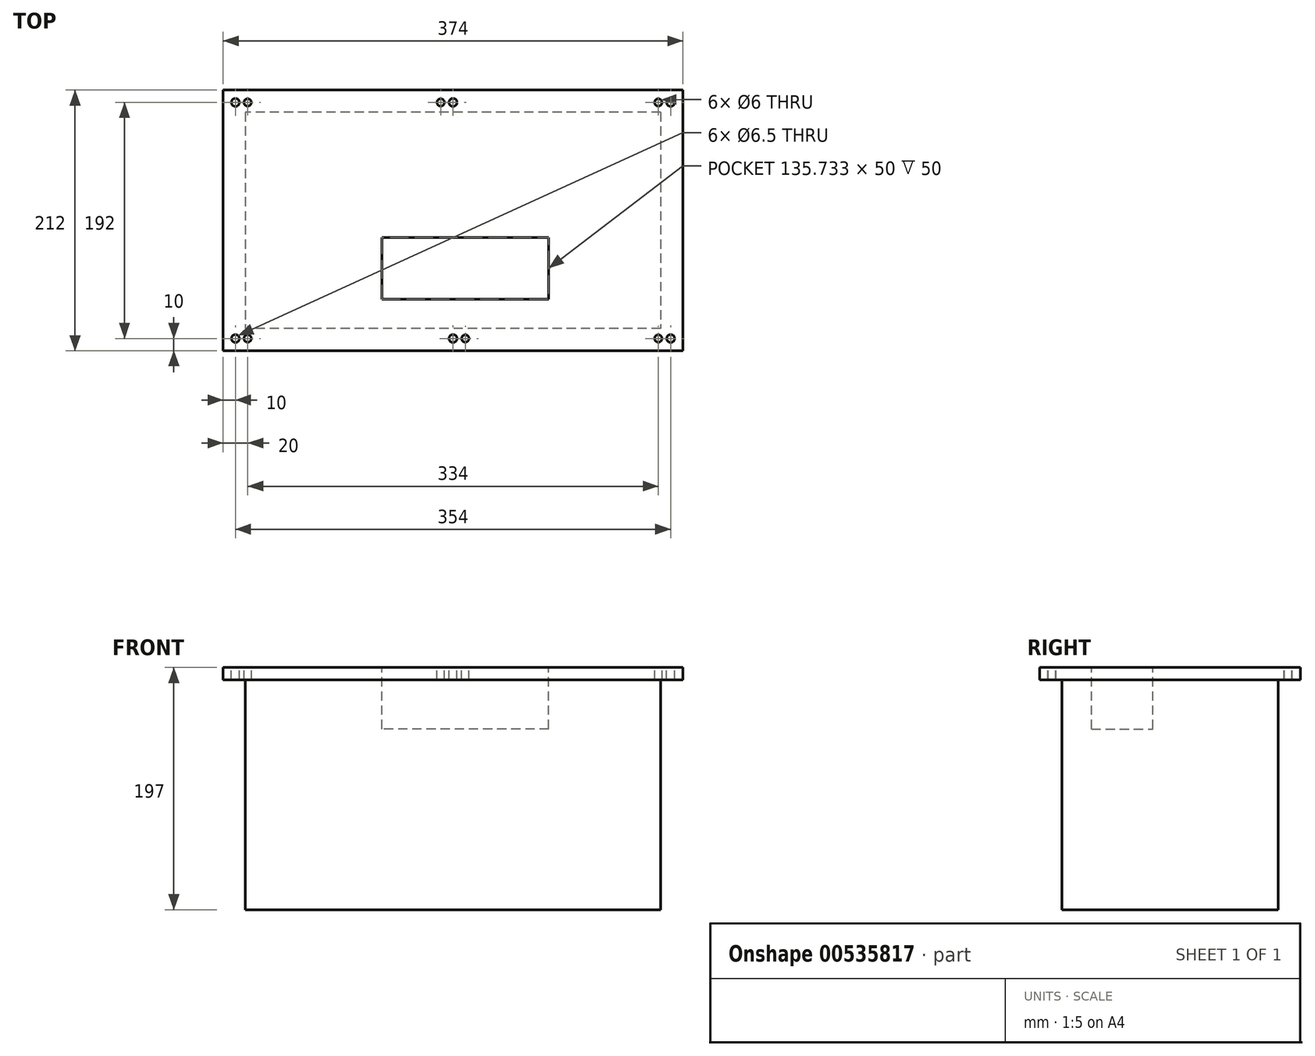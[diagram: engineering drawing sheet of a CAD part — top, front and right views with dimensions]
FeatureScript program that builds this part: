
annotation { "Feature Type Name" : "Feature", "Feature Type Description" : "" }
export const myFeature = defineFeature(function(context is Context, id is Id, definition is map)
    precondition{}
    {
        {
            var Q0;
            Q0=qCreatedBy(makeId("Top.planeOp"),FACE);
            var sketch = newSketch(context, id + "F0", { "sketchPlane" : qUnion([Q0])});
            skLineSegment(sketch, "E0.bottom", {"start": v(187, -106) * mm, "end": v(-187, -106) * mm});
            skLineSegment(sketch, "E0.top", {"start": v(187, 106) * mm, "end": v(-187, 106) * mm});
            skLineSegment(sketch, "E0.left", {"start": v(187, -106) * mm, "end": v(187, 106) * mm});
            skLineSegment(sketch, "E0.right", {"start": v(-187, -106) * mm, "end": v(-187, 106) * mm});
            skPoint(sketch, "E0.middle", {"position": v(0, 0) * mm});
            skSolve(sketch);
        }
        {
            var Q0;
            Q0=qSketchRegion(id+"F0",true);
            extrude(context, id + "F1", {"entities" : qUnion([Q0]), "depth" : 10 * mm});
        }
        {
            var Q0;
            Q0=makeQuery(id+"F1.opExtrude","CAP_FACE",FACE,{"disambiguationData":[OSD([sQuery(id+"F0.wireOp",EDGE,"E0.bottom"),sQuery(id+"F0.wireOp",EDGE,"E0.top"),sQuery(id+"F0.wireOp",EDGE,"E0.left"),sQuery(id+"F0.wireOp",EDGE,"E0.right")])],"isStart":true});
            var sketch = newSketch(context, id + "F2", { "sketchPlane" : qUnion([Q0])});
            skLineSegment(sketch, "E1.bottom", {"start": v(169, -88) * mm, "end": v(-169, -88) * mm});
            skLineSegment(sketch, "E1.top", {"start": v(169, 88) * mm, "end": v(-169, 88) * mm});
            skLineSegment(sketch, "E1.left", {"start": v(169, -88) * mm, "end": v(169, 88) * mm});
            skLineSegment(sketch, "E1.right", {"start": v(-169, -88) * mm, "end": v(-169, 88) * mm});
            skPoint(sketch, "E1.middle", {"position": v(0, 0) * mm});
            skSolve(sketch);
        }
        {
            var Q0;
            Q0=qSketchRegion(id+"F2",true);
            extrude(context, id + "F3", {"entities" : qUnion([Q0]), "operationType" : NewBodyOperationType.ADD, "depth" : 187 * mm});
        }
        {
            var Q0;
            Q0=makeQuery(id+"F1.opExtrude","CAP_FACE",FACE,{"disambiguationData":[OSD([sQuery(id+"F0.wireOp",EDGE,"E0.bottom"),sQuery(id+"F0.wireOp",EDGE,"E0.top"),sQuery(id+"F0.wireOp",EDGE,"E0.left"),sQuery(id+"F0.wireOp",EDGE,"E0.right")])],"isStart":false});
            var sketch = newSketch(context, id + "F4", { "sketchPlane" : qUnion([Q0])});
            skLineSegment(sketch, "E2.bottom", {"start": v(77.89, -63.9) * mm, "end": v(-57.85, -63.9) * mm});
            skLineSegment(sketch, "E2.top", {"start": v(77.89, -13.9) * mm, "end": v(-57.85, -13.9) * mm});
            skLineSegment(sketch, "E2.left", {"start": v(77.89, -63.9) * mm, "end": v(77.89, -13.9) * mm});
            skLineSegment(sketch, "E2.right", {"start": v(-57.85, -63.9) * mm, "end": v(-57.85, -13.9) * mm});
            skPoint(sketch, "E2.middle", {"position": v(10.02, -38.9) * mm});
            skSolve(sketch);
        }
        {
            var Q0;
            Q0=qSketchRegion(id+"F4",true);
            extrude(context, id + "F5", {"entities" : qUnion([Q0]), "operationType" : NewBodyOperationType.REMOVE, "oppositeDirection" : true, "depth" : 50 * mm});
        }
        {
            var Q0;
            {var subQ0=sQuery(id+"F0.wireOp",EDGE,"E0.left");var subQ1=sQuery(id+"F0.wireOp",EDGE,"E0.top");var subQ2=sQuery(id+"F0.wireOp",EDGE,"E0.right");var subQ3=sQuery(id+"F0.wireOp",EDGE,"E0.bottom");Q0=makeQuery(id+"F5.boolean.opBoolean","SPLIT",FACE,{"disambiguationData":[TD([makeQuery(id+"F1.opExtrude","SWEPT_FACE",FACE,{"disambiguationData":[OSD([subQ3])]})])],"derivedFrom":makeQuery(id+"F1.opExtrude","CAP_FACE",FACE,{"disambiguationData":[OSD([subQ3,subQ1,subQ0,subQ2])],"isStart":false})});}
            var sketch = newSketch(context, id + "F6", { "sketchPlane" : qUnion([Q0])});
            skPoint(sketch, "E3", {"position": v(-177, 96) * mm});
            skPoint(sketch, "E4", {"position": v(-167, 96) * mm});
            skPoint(sketch, "E5", {"position": v(-10, 96) * mm});
            skPoint(sketch, "E6", {"position": v(0, 96) * mm});
            skPoint(sketch, "E7", {"position": v(167, 96) * mm});
            skPoint(sketch, "E8", {"position": v(177, 96) * mm});
            skPoint(sketch, "E9.MirrorP", {"position": v(177, -96) * mm});
            skPoint(sketch, "E10.MirrorP", {"position": v(167, -96) * mm});
            skPoint(sketch, "E11.MirrorP", {"position": v(-167, -96) * mm});
            skPoint(sketch, "E12.MirrorP", {"position": v(-177, -96) * mm});
            skPoint(sketch, "E13", {"position": v(0, -96) * mm});
            skPoint(sketch, "E14", {"position": v(10, -96) * mm});
            skSolve(sketch);
        }
        {
            var Q0;
            Q0=sQuery(id+"F6.wireOp",VERTEX,"E4");
            var Q1;
            Q1=sQuery(id+"F6.wireOp",VERTEX,"E11.MirrorP");
            var Q2;
            Q2=sQuery(id+"F6.wireOp",VERTEX,"E10.MirrorP");
            var Q3;
            Q3=sQuery(id+"F6.wireOp",VERTEX,"E7");
            var Q4;
            Q4=sQuery(id+"F6.wireOp",VERTEX,"E5");
            var Q5;
            Q5=sQuery(id+"F6.wireOp",VERTEX,"E14");
            var Q6;
            Q6=makeQuery(id+"F1.opExtrude","SWEPT_BODY",BODY,{"disambiguationData":[OSD([sQuery(id+"F0.wireOp",EDGE,"E0.bottom"),sQuery(id+"F0.wireOp",EDGE,"E0.top"),sQuery(id+"F0.wireOp",EDGE,"E0.left"),sQuery(id+"F0.wireOp",EDGE,"E0.right")])]});
            hole(context, id + "F7", {"style" : HoleStyle.SIMPLE, "endStyle" : HoleEndStyle.BLIND, "holeDiameter" : 6 * mm, "holeDepth" : 10 * mm, "tappedDepth" : 12 * mm, "tapClearance" : 3, "locations" : qUnion([Q0, Q1, Q2, Q3, Q4, Q5]), "scope" : qUnion([Q6])});
        }
        {
            var Q0;
            Q0=sQuery(id+"F6.wireOp",VERTEX,"E3");
            var Q1;
            Q1=sQuery(id+"F6.wireOp",VERTEX,"E12.MirrorP");
            var Q2;
            Q2=sQuery(id+"F6.wireOp",VERTEX,"E13");
            var Q3;
            Q3=sQuery(id+"F6.wireOp",VERTEX,"E6");
            var Q4;
            Q4=sQuery(id+"F6.wireOp",VERTEX,"E8");
            var Q5;
            Q5=sQuery(id+"F6.wireOp",VERTEX,"E9.MirrorP");
            var Q6;
            Q6=makeQuery(id+"F1.opExtrude","SWEPT_BODY",BODY,{"disambiguationData":[OSD([sQuery(id+"F0.wireOp",EDGE,"E0.bottom"),sQuery(id+"F0.wireOp",EDGE,"E0.top"),sQuery(id+"F0.wireOp",EDGE,"E0.left"),sQuery(id+"F0.wireOp",EDGE,"E0.right")])]});
            hole(context, id + "F8", {"style" : HoleStyle.SIMPLE, "endStyle" : HoleEndStyle.BLIND, "holeDiameter" : 6.5 * mm, "holeDepth" : 10 * mm, "tappedDepth" : 12 * mm, "tapClearance" : 3, "locations" : qUnion([Q0, Q1, Q2, Q3, Q4, Q5]), "scope" : qUnion([Q6])});
        }
    });
